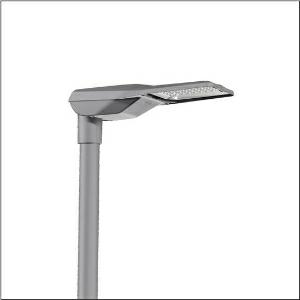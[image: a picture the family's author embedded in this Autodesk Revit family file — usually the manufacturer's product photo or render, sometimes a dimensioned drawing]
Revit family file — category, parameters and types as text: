
# Revit family: streetlight_sl_21_iq_mini___st0_8a_5xe2c21g08hb_0b1a
name_source: partatom
category: Lighting Fixtures
units: mm (PartAtom-declared; Revit-internal decimal feet)

## family parameters
Cut with Voids When Loaded = No
Host = Face
Light Source = No
Part Type = Normal
Room Calculation Point = No
Round Connector Dimension = Use Diameter
Shared = No

## types (1)
- --- (1 x LED, 7830 lm, 70.9 W, 2200K)
    Apparent Load = 71 VA
    CIE Flux Codes = 38 75 97 100 100
    Color Rendering = 70
    Color Temperature = 2200K
    Default Elevation = 1800 mm
    Description = Streetlight SL 21 iQ mini, mast luminaire, primary light control with lens, of PMMA, primary optical cover: cover, of toughened safety glass, transparent, light distribution: ST0.8a, light emission: direct distribution, primary light characteristic: asymmetric, installation type: post-top, side-entry, LED, High Power LED, rated luminous flux: 7.830lm, luminous efficacy: 110lm/W, light colour: 722, colour temperature: 2200K, control gear: iQ Street-Remote, control: Street-Remote, Auto-Match, Temp-Guard, Lumen-Switch, Night-Set, Smart-Wire, Light-Fading, Desk-Remote (wireless, voltage-free reading and setting of iQ features in the workshop via application-optimized NFC function/RFID function), optimised constant luminous flux control (CLO 2.0), pre-setting: linear dimming characteristic, mains connection: 220..240V, AC, 50/60Hz, start of lifetime: 71W, end of service life: 75W, reduction: 31W, luminaire housing, of diecast aluminium, powder-coated, SITECO metallic grey (DB 702S), corrosivity category C5 high according to DIN EN ISO 12944, please order mast flange separately, inclination adjustable: 0°, 5°, 10°, 15°, sealing non-destructively replaceable, multi-level sealing system, length: 628mm, width: 235mm, height: 110mm, mast flange for spigot size: 42mm (side-entry): 5XC10008XM4, 60/48mm (side-entry/post-top): 5XC10108XM2, 76/60mm (side-entry/post-top): 5XC10108XM1, mounting height: 4..8m, protection rating (complete): IP66, insulation class (complete): insulation class II (safety insulation), certification: CE, ENEC, ENEC+, VDE, impact resistance: IK10, permissible operating ambient temperature for outdoor applications: -40..+50°C, standard-compliant lighting for roads and squares, packaging unit: 1 piece

Light Distribution: ST0.8a
    Height = 110 mm
    Lamp = 1 x LED
    Lamp Light Flux = 7830 lm
    Lamp Power = 70.9 W
    Lamp count = 1
    Length = 625 mm
    Luminous efficacy = 110 lm/W
    Manufacturer = Siteco
    ModVariant = No
    Model = 5XE2C21G08HB
    Number of Poles = 1
    OnlyDefault = Yes
    Power Factor = 1
    Product Name = Streetlight SL 21 iQ mini | ST0.8a
    Product group = mast luminaire | pylon top
    ProductGroupID = 6100
    Protection Class = Protection class II
    Protection Degree = IP 66
    RLX_Detail_Level = 1
    RLX_Emergency_Light_Flux = 0 lm
    RLX_Emergency_Type = 0
    RLX_Emergency_Type_DB = No
    RlxData = <blob elided: 26269 chars, md5=25f2ae27>
    Socket = socket
    Standby Power = 0 W
    System Light Flux = 7830 lm
    System Power = 71 W
    Type Comments = factory setting: luminous flux: 100 % | dim-lin: 254 | 711 mA
    Type Image = l_1003519.jpg
    URL = http://relux.com
    VarID = @adj_156995
    Voltage = 0 V
    Weight = 0.00 kg
    Width = 234 mm

## geometry (parser evidence)
native form markers: Blend x4, Sweep x10
no freeform markers — native parametric forms only
